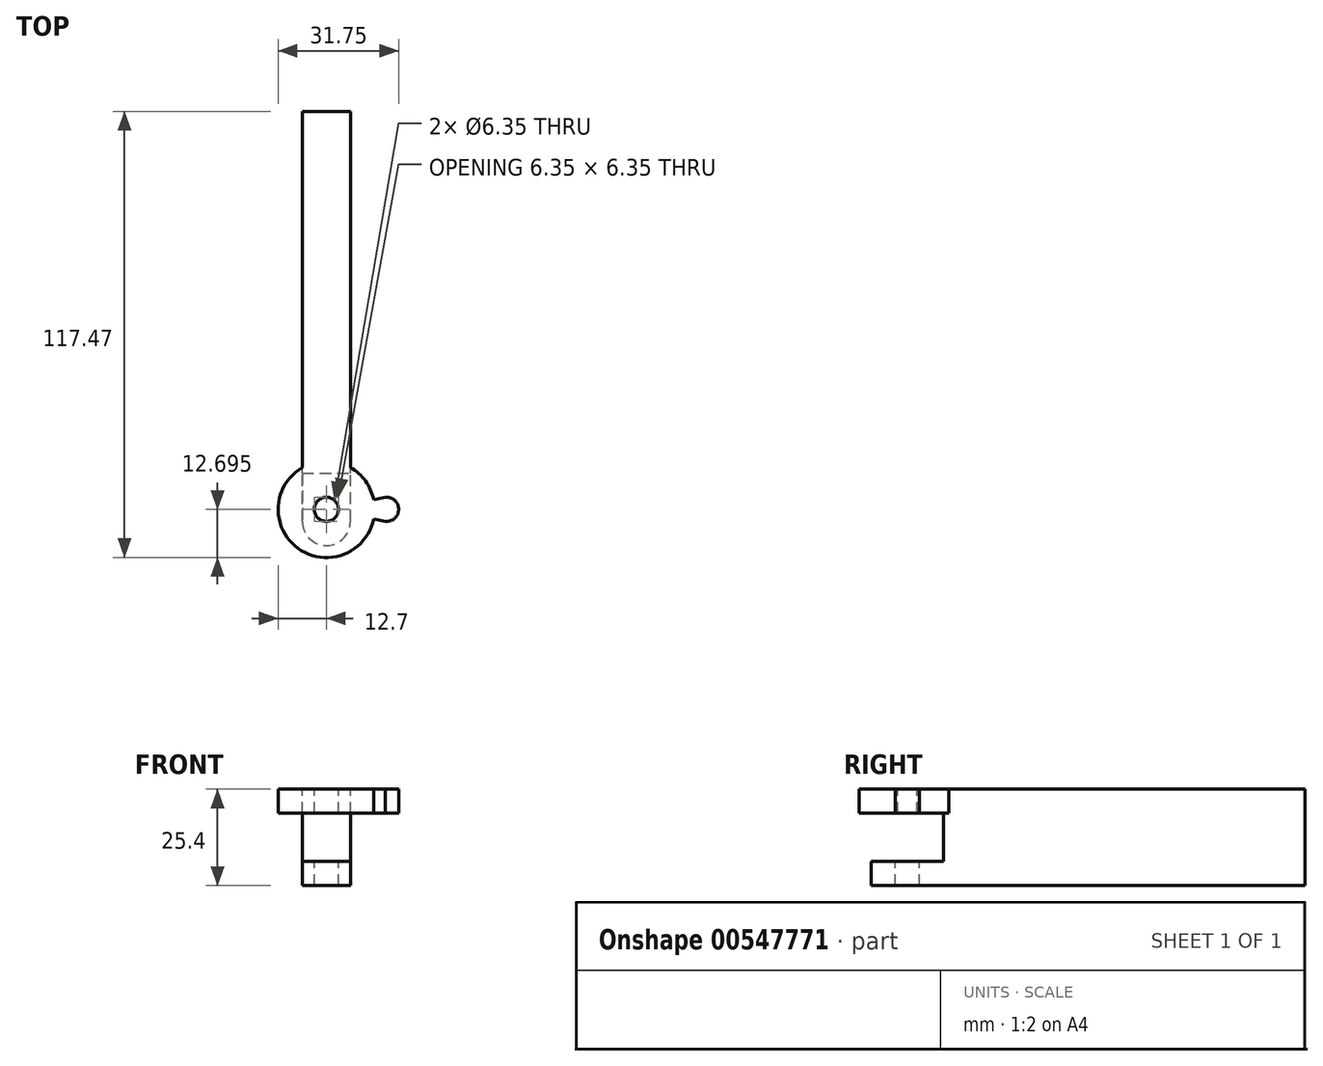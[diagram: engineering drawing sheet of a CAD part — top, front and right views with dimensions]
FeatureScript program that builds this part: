
annotation { "Feature Type Name" : "Feature", "Feature Type Description" : "" }
export const myFeature = defineFeature(function(context is Context, id is Id, definition is map)
    precondition{}
    {
        {
            var Q0;
            Q0=qCreatedBy(makeId("Top.planeOp"),FACE);
            var sketch = newSketch(context, id + "F0", { "sketchPlane" : qUnion([Q0])});
            skLineSegment(sketch, "E0.bottom", {"start": v(0, 0) * mm, "end": v(12.7, 0) * mm});
            skLineSegment(sketch, "E0.top", {"start": v(0, 114.3) * mm, "end": v(12.7, 114.3) * mm});
            skLineSegment(sketch, "E0.left", {"start": v(0, 0) * mm, "end": v(0, 114.3) * mm});
            skLineSegment(sketch, "E0.right", {"start": v(12.7, 0) * mm, "end": v(12.7, 114.3) * mm});
            skSolve(sketch);
        }
        {
            var Q0;
            Q0 = qSketchRegion(id + "F0", true);
            extrude(context, id + "F1", {"entities" : qUnion([Q0]), "depth" : 25.4 * mm, "offsetDistance" : 25.4 * mm});
        }
        {
            var Q0;
            Q0=makeQuery(id+"F1.opExtrude","SWEPT_FACE",FACE,{"disambiguationData":[OSD([sQuery(id+"F0.wireOp",EDGE,"E0.right")])]});
            var sketch = newSketch(context, id + "F2", { "sketchPlane" : qUnion([Q0])});
            skLineSegment(sketch, "E1.bottom", {"start": v(0, 6.35) * mm, "end": v(19.05, 6.35) * mm});
            skLineSegment(sketch, "E1.top", {"start": v(0, 19.05) * mm, "end": v(19.05, 19.05) * mm});
            skLineSegment(sketch, "E1.left", {"start": v(0, 6.35) * mm, "end": v(0, 19.05) * mm});
            skLineSegment(sketch, "E1.right", {"start": v(19.05, 6.35) * mm, "end": v(19.05, 19.05) * mm});
            skSolve(sketch);
        }
        {
            var Q0;
            Q0 = qSketchRegion(id + "F2", true);
            extrude(context, id + "F3", {"entities" : qUnion([Q0]), "operationType" : NewBodyOperationType.REMOVE, "endBound" : BoundingType.THROUGH_ALL, "oppositeDirection" : true, "depth" : 25.4 * mm, "offsetDistance" : 25.4 * mm});
        }
        {
            var Q0;
            {var subQ0=sQuery(id+"F0.wireOp",EDGE,"E0.bottom");var subQ1=sQuery(id+"F0.wireOp",EDGE,"E0.right");Q0=makeQuery(id+"F3.boolean.opBoolean","SPLIT",EDGE,{"disambiguationData":[TD([makeQuery(id+"F3.opExtrude","SWEPT_FACE",FACE,{"disambiguationData":[OSD([sQuery(id+"F2.wireOp",EDGE,"E1.top")])]})])],"derivedFrom":makeQuery(id+"F1.opExtrude","SWEPT_EDGE",EDGE,{"disambiguationData":[OSD([subQ0,subQ1])]})});}
            var Q1;
            {var subQ0=sQuery(id+"F0.wireOp",EDGE,"E0.bottom");var subQ1=sQuery(id+"F0.wireOp",EDGE,"E0.right");Q1=makeQuery(id+"F3.boolean.opBoolean","SPLIT",EDGE,{"disambiguationData":[TD([makeQuery(id+"F3.opExtrude","SWEPT_FACE",FACE,{"disambiguationData":[OSD([sQuery(id+"F2.wireOp",EDGE,"E1.bottom")])]})])],"derivedFrom":makeQuery(id+"F1.opExtrude","SWEPT_EDGE",EDGE,{"disambiguationData":[OSD([subQ0,subQ1])]})});}
            var Q2;
            {var subQ0=sQuery(id+"F0.wireOp",EDGE,"E0.bottom");var subQ1=sQuery(id+"F0.wireOp",EDGE,"E0.left");Q2=makeQuery(id+"F3.boolean.opBoolean","SPLIT",EDGE,{"disambiguationData":[TD([makeQuery(id+"F3.opExtrude","SWEPT_FACE",FACE,{"disambiguationData":[OSD([sQuery(id+"F2.wireOp",EDGE,"E1.bottom")])]})])],"derivedFrom":makeQuery(id+"F1.opExtrude","SWEPT_EDGE",EDGE,{"disambiguationData":[OSD([subQ0,subQ1])]})});}
            var Q3;
            {var subQ0=sQuery(id+"F0.wireOp",EDGE,"E0.bottom");var subQ1=sQuery(id+"F0.wireOp",EDGE,"E0.left");Q3=makeQuery(id+"F3.boolean.opBoolean","SPLIT",EDGE,{"disambiguationData":[TD([makeQuery(id+"F3.opExtrude","SWEPT_FACE",FACE,{"disambiguationData":[OSD([sQuery(id+"F2.wireOp",EDGE,"E1.top")])]})])],"derivedFrom":makeQuery(id+"F1.opExtrude","SWEPT_EDGE",EDGE,{"disambiguationData":[OSD([subQ0,subQ1])]})});}
            fillet(context, id + "F4", {"entities" : qUnion([Q0, Q1, Q2, Q3]), "radius" : 6.35 * mm, "tangentPropagation" : true, "allowEdgeOverflow" : false});
        }
        {
            var Q0;
            Q0=makeQuery(id+"F1.opExtrude","CAP_FACE",FACE,{"disambiguationData":[OSD([sQuery(id+"F0.wireOp",EDGE,"E0.bottom"),sQuery(id+"F0.wireOp",EDGE,"E0.top"),sQuery(id+"F0.wireOp",EDGE,"E0.left"),sQuery(id+"F0.wireOp",EDGE,"E0.right")])],"isStart":false});
            var sketch = newSketch(context, id + "F5", { "sketchPlane" : qUnion([Q0])});
            skCircle(sketch, "E2", {"center": v(6.35, 9.53) * mm, "radius": 3.18 * mm});
            skPoint(sketch, "E2.centerSnap0", {"position": v(6.35, 0) * mm});
            skSolve(sketch);
        }
        {
            var Q0;
            Q0 = qSketchRegion(id + "F5", true);
            extrude(context, id + "F6", {"entities" : qUnion([Q0]), "operationType" : NewBodyOperationType.REMOVE, "endBound" : BoundingType.THROUGH_ALL, "oppositeDirection" : true, "depth" : 25.4 * mm, "offsetDistance" : 25.4 * mm});
        }
        {
            var Q0;
            Q0=makeQuery(id+"F1.opExtrude","CAP_FACE",FACE,{"disambiguationData":[OSD([sQuery(id+"F0.wireOp",EDGE,"E0.bottom"),sQuery(id+"F0.wireOp",EDGE,"E0.top"),sQuery(id+"F0.wireOp",EDGE,"E0.left"),sQuery(id+"F0.wireOp",EDGE,"E0.right")])],"isStart":false});
            var sketch = newSketch(context, id + "F7", { "sketchPlane" : qUnion([Q0])});
            skArc(sketch, "E3", {"start": v(0, 20.52) * mm, "mid": v(6.35, -3.18) * mm, "end": v(12.7, 20.52) * mm});
            skLineSegment(sketch, "E4.0", {"start": v(0, 6.35) * mm, "end": v(0, 20.52) * mm});
            skLineSegment(sketch, "E4.1", {"start": v(12.7, 6.35) * mm, "end": v(12.7, 20.52) * mm});
            skArc(sketch, "E4.2", {"start": v(0, 6.35) * mm, "mid": v(6.35, 0) * mm, "end": v(12.7, 6.35) * mm});
            skPoint(sketch, "E5.orphan", {"position": v(0, 114.3) * mm});
            skPoint(sketch, "E6.orphan", {"position": v(12.7, 114.3) * mm});
            skSolve(sketch);
        }
        {
            var Q0;
            Q0 = qSketchRegion(id + "F7", true);
            var Q1;
            Q1=makeQuery(id+"F3.boolean.opBoolean","COPY",FACE,{"derivedFrom":makeQuery(id+"F3.opExtrude","SWEPT_FACE",FACE,{"disambiguationData":[OSD([sQuery(id+"F2.wireOp",EDGE,"E1.top")])]})});
            var Q2;
            Q2=makeQuery(id+"F1.opExtrude","SWEPT_BODY",BODY,{"disambiguationData":[OSD([sQuery(id+"F0.wireOp",EDGE,"E0.bottom"),sQuery(id+"F0.wireOp",EDGE,"E0.top"),sQuery(id+"F0.wireOp",EDGE,"E0.left"),sQuery(id+"F0.wireOp",EDGE,"E0.right")])]});
            extrude(context, id + "F8", {"entities" : qUnion([Q0]), "operationType" : NewBodyOperationType.ADD, "endBound" : BoundingType.UP_TO_SURFACE, "oppositeDirection" : true, "depth" : 25.4 * mm, "endBoundEntityFace" : qUnion([Q1]), "endBoundEntityBody" : qUnion([Q2]), "offsetDistance" : 25.4 * mm});
        }
        {
            var Q0;
            Q0=makeQuery(id+"F8.boolean.opBoolean","MERGE",FACE,{"derivedFrom":[makeQuery(id+"F1.opExtrude","CAP_FACE",FACE,{"disambiguationData":[OSD([sQuery(id+"F0.wireOp",EDGE,"E0.bottom"),sQuery(id+"F0.wireOp",EDGE,"E0.top"),sQuery(id+"F0.wireOp",EDGE,"E0.left"),sQuery(id+"F0.wireOp",EDGE,"E0.right")])],"isStart":false}),makeQuery(id+"F8.opExtrude","CAP_FACE",FACE,{"disambiguationData":[OSD([sQuery(id+"F7.wireOp",EDGE,"E3"),sQuery(id+"F7.wireOp",EDGE,"E4.0"),sQuery(id+"F7.wireOp",EDGE,"E4.1"),sQuery(id+"F7.wireOp",EDGE,"E4.2")])],"isStart":true})]});
            var sketch = newSketch(context, id + "F9", { "sketchPlane" : qUnion([Q0])});
            skArc(sketch, "E7", {"start": v(21.9, 12.68) * mm, "mid": v(21.9, 12.7) * mm, "end": v(21.9, 12.7) * mm});
            skArc(sketch, "E8", {"start": v(21.59, 6.41) * mm, "mid": v(25.4, 9.53) * mm, "end": v(21.59, 12.64) * mm});
            skLineSegment(sketch, "E9", {"start": v(18.8, 12.07) * mm, "end": v(21.9, 12.7) * mm});
            skLineSegment(sketch, "E10", {"start": v(18.8, 6.99) * mm, "end": v(21.9, 6.35) * mm});
            skArc(sketch, "E11.trimOffspring", {"start": v(21.9, 6.35) * mm, "mid": v(21.9, 6.36) * mm, "end": v(21.9, 6.37) * mm});
            skArc(sketch, "E12.0", {"start": v(18.8, 6.99) * mm, "mid": v(19.05, 9.52) * mm, "end": v(18.8, 12.06) * mm});
            skSolve(sketch);
        }
        {
            var Q0;
            Q0 = qSketchRegion(id + "F9", true);
            var Q1;
            {var subQ0=sQuery(id+"F2.wireOp",EDGE,"E1.top");Q1=makeQuery(id+"F8.boolean.opBoolean","MERGE",FACE,{"derivedFrom":[makeQuery(id+"F3.boolean.opBoolean","COPY",FACE,{"derivedFrom":makeQuery(id+"F3.opExtrude","SWEPT_FACE",FACE,{"disambiguationData":[OSD([subQ0])]})}),makeQuery(id+"F8.opExtrude","CAP_FACE",FACE,{"disambiguationData":[OSD([subQ0])],"isStart":false})]});}
            extrude(context, id + "F10", {"entities" : qUnion([Q0]), "operationType" : NewBodyOperationType.ADD, "endBound" : BoundingType.UP_TO_SURFACE, "oppositeDirection" : true, "depth" : 25.4 * mm, "endBoundEntityFace" : qUnion([Q1]), "offsetDistance" : 25.4 * mm});
        }
    });
